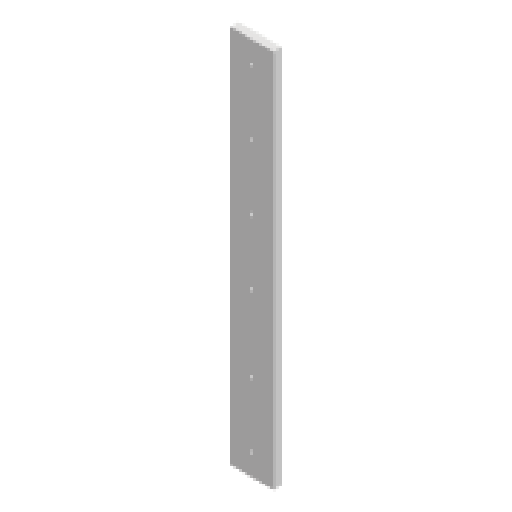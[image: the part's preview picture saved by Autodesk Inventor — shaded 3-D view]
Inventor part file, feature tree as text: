
AUTODESK INVENTOR PART (.ipt)
format: ipt  version: 2024 (Build 280153000, 153)  size: 103,424 bytes
history: native  units: in
note: dims shown in document units (in); Inventor stores cm internally (conversion verified against a paired STEP export)
features: extrude x2, sketch x2
ambient origin geometry x8: Origin, YZ Plane, XZ Plane, XY Plane, X Axis, Y Axis, Z Axis, Center Point
bodies: Solid1 (feature_tree)
feature tree (4):
  extrude  "Extrusion1"  Depth=34.4488in
  extrude  "Extrusion2"  Depth=0.748in
  sketch  "Sketch1"  dims[d0=3.937in d1=34.4488in]
  sketch  "Sketch2"  dims[d2=0.748in d3=0.0in d4=1.9685in d5=5.9055in d6=5.9055in d7=5.9055in d8=6.8898in d9=5.9055in d10=1.9685in d11=0.315in d12=0.315in d13=0.315in d14=0.315in d15=0.315in d16=0.315in d17=0.4331in d18=0.0in]
